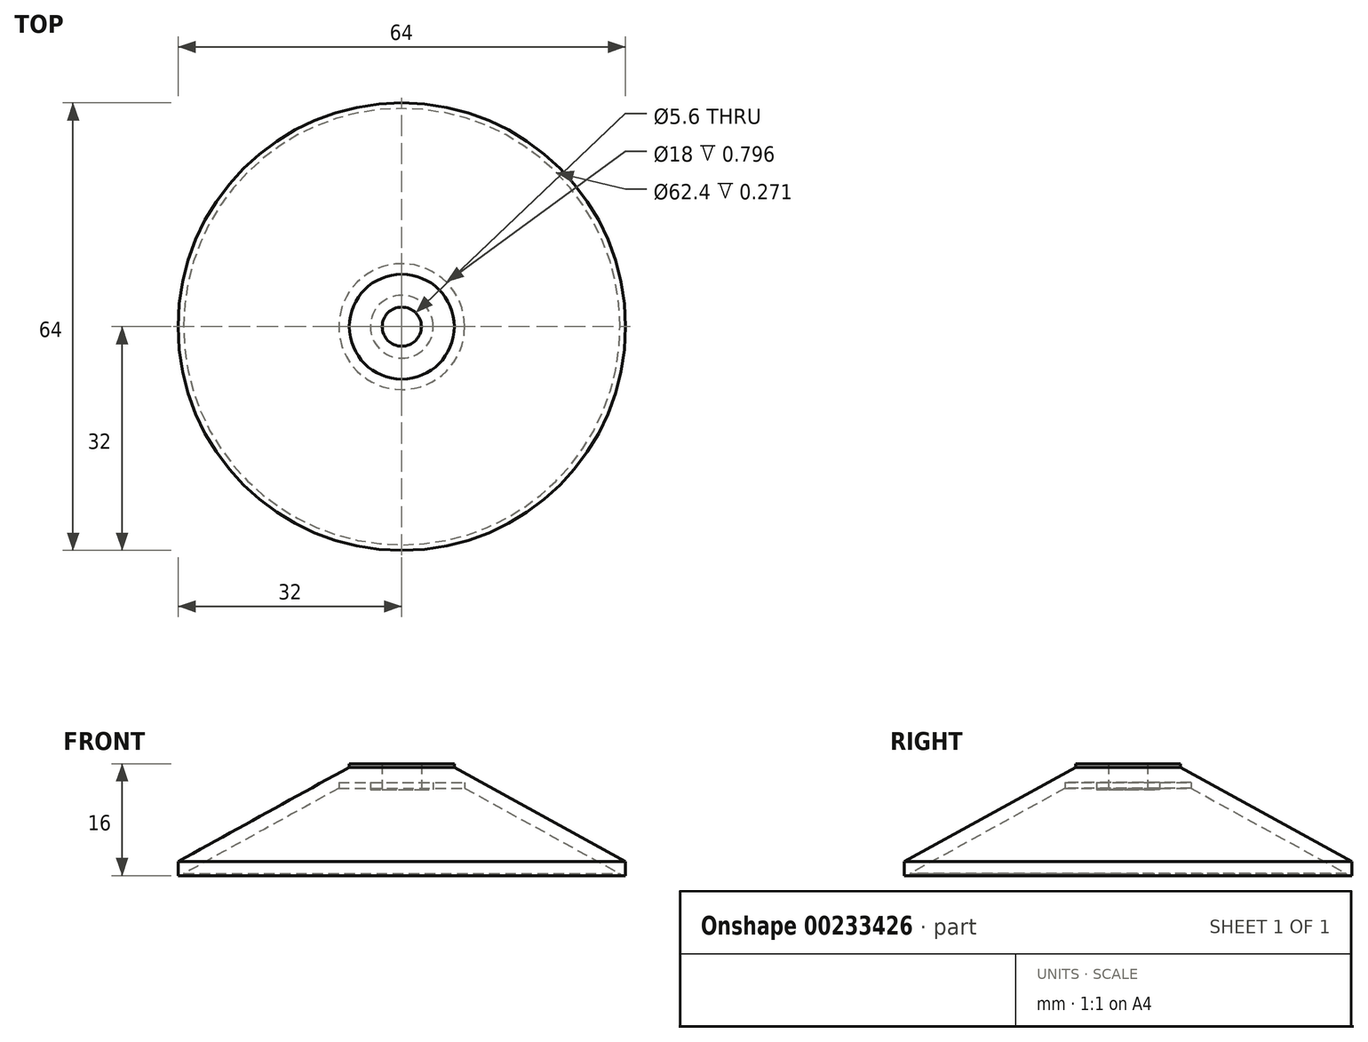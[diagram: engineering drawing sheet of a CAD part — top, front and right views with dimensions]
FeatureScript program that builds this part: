
annotation { "Feature Type Name" : "Feature", "Feature Type Description" : "" }
export const myFeature = defineFeature(function(context is Context, id is Id, definition is map)
    precondition{}
    {
        {
            var Q0;
            Q0=qCreatedBy(makeId("Front.planeOp"),FACE);
            var sketch = newSketch(context, id + "F0", { "sketchPlane" : qUnion([Q0])});
            skLineSegment(sketch, "E0", {"start": v(0, 0) * mm, "end": v(70.35, 0) * mm, "construction": true});
            skLineSegment(sketch, "E1", {"start": v(0, 0) * mm, "end": v(0, 35.6) * mm, "construction": true});
            skLineSegment(sketch, "E2", {"start": v(0, 16) * mm, "end": v(7.5, 16) * mm});
            skLineSegment(sketch, "E3", {"start": v(32, 2) * mm, "end": v(32, 0) * mm});
            skLineSegment(sketch, "E4", {"start": v(7.5, 16) * mm, "end": v(7.5, 15.5) * mm});
            skLineSegment(sketch, "E5", {"start": v(7.5, 15.5) * mm, "end": v(32, 2) * mm});
            skLineSegment(sketch, "E6", {"start": v(9, 12.5) * mm, "end": v(31.2, 0.27) * mm});
            skLineSegment(sketch, "E7", {"start": v(32, 0) * mm, "end": v(31.2, 0) * mm});
            skLineSegment(sketch, "E8", {"start": v(31.2, 0) * mm, "end": v(31.2, 0.27) * mm});
            skLineSegment(sketch, "E9", {"start": v(2.8, 16) * mm, "end": v(2.8, 12.3) * mm});
            skLineSegment(sketch, "E10", {"start": v(2.8, 12.3) * mm, "end": v(4.5, 12.3) * mm});
            skLineSegment(sketch, "E11", {"start": v(4.5, 12.3) * mm, "end": v(4.5, 13.3) * mm});
            skLineSegment(sketch, "E12", {"start": v(9, 12.5) * mm, "end": v(9, 13.3) * mm});
            skLineSegment(sketch, "E13", {"start": v(9, 13.3) * mm, "end": v(4.5, 13.3) * mm});
            skSolve(sketch);
        }
        {
            var Q0;
            Q0=makeQuery(id+"F0.imprint","IMPRINT",FACE,{"disambiguationData":[TD([[makeQuery(id+"F0.imprint","IMPRINT",EDGE,{"derivedFrom":sQuery(id+"F0.wireOp",EDGE,"E3")}),-1.0]])]});
            var Q1;
            Q1=sQuery(id+"F0.wireOp",EDGE,"E1");
            revolve(context, id + "F1", {"entities" : qUnion([Q0]), "axis" : qUnion([Q1]), "revolveType" : RevolveType.FULL});
        }
    });
